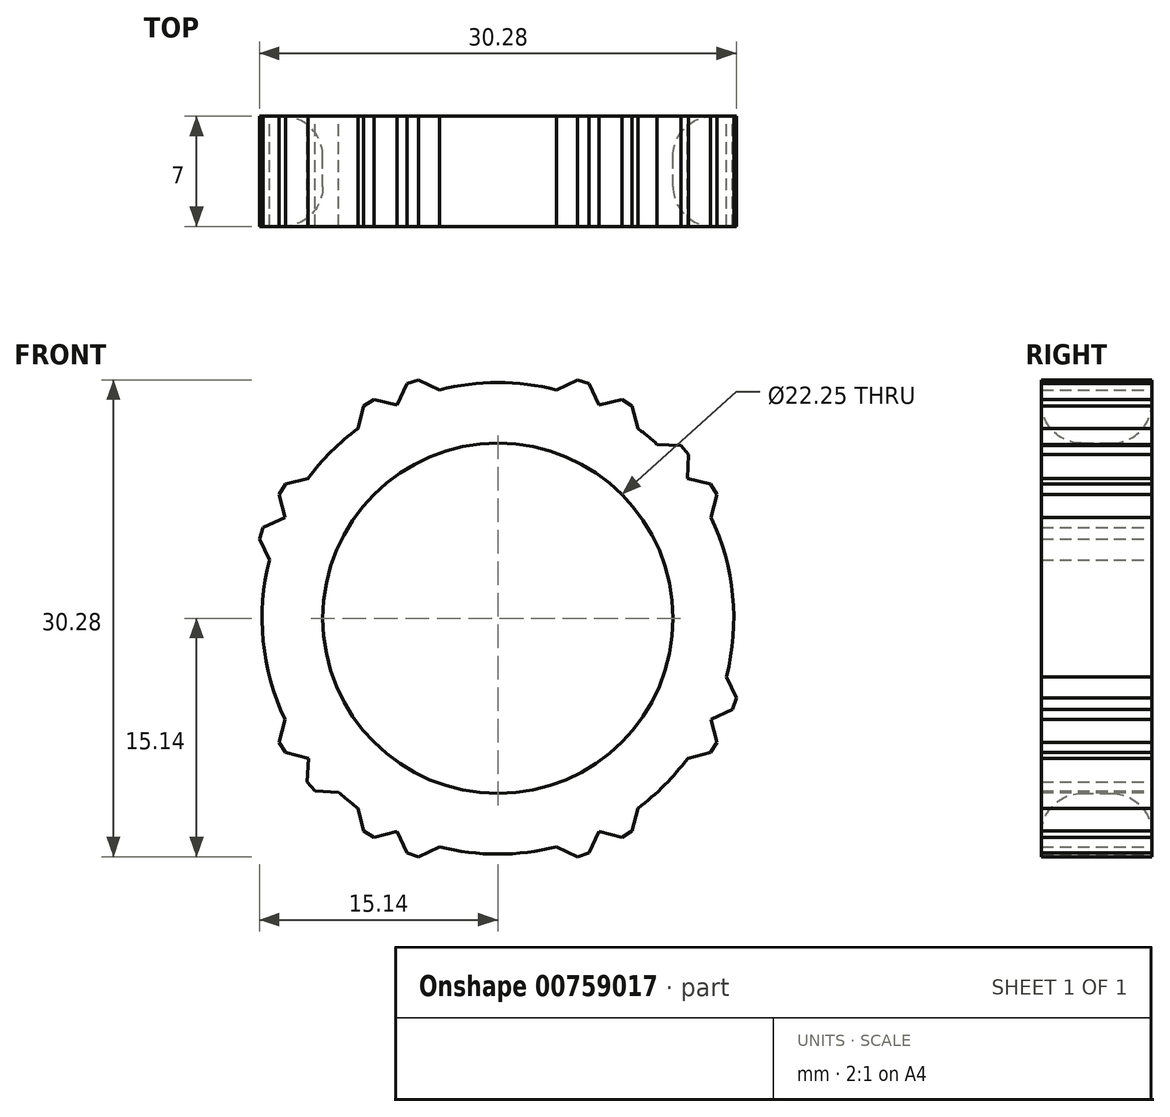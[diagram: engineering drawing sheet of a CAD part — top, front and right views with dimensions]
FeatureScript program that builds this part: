
annotation { "Feature Type Name" : "Feature", "Feature Type Description" : "" }
export const myFeature = defineFeature(function(context is Context, id is Id, definition is map)
    precondition{}
    {
        {
            var Q0;
            Q0=qCreatedBy(makeId("Front.planeOp"),FACE);
            var sketch = newSketch(context, id + "F0", { "sketchPlane" : qUnion([Q0])});
            skCircle(sketch, "E0", {"center": v(0, 0) * mm, "radius": 11.13 * mm});
            skCircle(sketch, "E1", {"center": v(0, 0) * mm, "radius": 14.98 * mm});
            skLineSegment(sketch, "E2", {"start": v(13.53, 6.42) * mm, "end": v(13.9, 7.88) * mm});
            skLineSegment(sketch, "E3", {"start": v(13.5, 8.52) * mm, "end": v(12.03, 8.89) * mm});
            skLineSegment(sketch, "E4", {"start": v(13.5, 8.52) * mm, "end": v(13.9, 7.88) * mm});
            skLineSegment(sketch, "E5.MirrorCS", {"start": v(-13.5, 8.52) * mm, "end": v(-12.03, 8.89) * mm});
            skLineSegment(sketch, "E6.MirrorCS", {"start": v(-13.53, 6.42) * mm, "end": v(-13.9, 7.88) * mm});
            skLineSegment(sketch, "E7.MirrorCS", {"start": v(-13.5, 8.52) * mm, "end": v(-13.9, 7.88) * mm});
            skLineSegment(sketch, "E8.MirrorCS", {"start": v(13.5, -8.52) * mm, "end": v(12.03, -8.89) * mm});
            skLineSegment(sketch, "E9.MirrorCS", {"start": v(13.53, -6.42) * mm, "end": v(13.9, -7.88) * mm});
            skLineSegment(sketch, "E10.MirrorCS", {"start": v(13.5, -8.52) * mm, "end": v(13.9, -7.88) * mm});
            skLineSegment(sketch, "E11.MirrorCS", {"start": v(-13.5, -8.52) * mm, "end": v(-12.03, -8.89) * mm});
            skLineSegment(sketch, "E12.MirrorCS", {"start": v(-13.53, -6.42) * mm, "end": v(-13.9, -7.88) * mm});
            skLineSegment(sketch, "E13.MirrorCS", {"start": v(-13.5, -8.52) * mm, "end": v(-13.9, -7.88) * mm});
            skLineSegment(sketch, "E14.MirrorCS", {"start": v(8.52, 13.5) * mm, "end": v(8.89, 12.03) * mm});
            skLineSegment(sketch, "E15.MirrorCS", {"start": v(6.42, 13.53) * mm, "end": v(7.88, 13.9) * mm});
            skLineSegment(sketch, "E16.MirrorCS", {"start": v(8.52, 13.5) * mm, "end": v(7.88, 13.9) * mm});
            skLineSegment(sketch, "E17.MirrorCS", {"start": v(-6.42, 13.53) * mm, "end": v(-7.88, 13.9) * mm});
            skLineSegment(sketch, "E18.MirrorCS", {"start": v(-8.52, 13.5) * mm, "end": v(-8.89, 12.03) * mm});
            skLineSegment(sketch, "E19.MirrorCS", {"start": v(-8.52, 13.5) * mm, "end": v(-7.88, 13.9) * mm});
            skLineSegment(sketch, "E20.MirrorCS", {"start": v(-8.52, -13.5) * mm, "end": v(-8.89, -12.03) * mm});
            skLineSegment(sketch, "E21.MirrorCS", {"start": v(-8.52, -13.5) * mm, "end": v(-7.88, -13.9) * mm});
            skLineSegment(sketch, "E22.MirrorCS", {"start": v(-6.42, -13.53) * mm, "end": v(-7.88, -13.9) * mm});
            skLineSegment(sketch, "E23.MirrorCS", {"start": v(8.52, -13.5) * mm, "end": v(8.89, -12.03) * mm});
            skLineSegment(sketch, "E24.MirrorCS", {"start": v(6.42, -13.53) * mm, "end": v(7.88, -13.9) * mm});
            skLineSegment(sketch, "E25.MirrorCS", {"start": v(8.52, -13.5) * mm, "end": v(7.88, -13.9) * mm});
            skLineSegment(sketch, "E26.MirrorCS", {"start": v(5.05, 15.14) * mm, "end": v(3.69, 14.5) * mm});
            skLineSegment(sketch, "E27.MirrorCS", {"start": v(6.42, 13.53) * mm, "end": v(5.78, 14.9) * mm});
            skLineSegment(sketch, "E28.MirrorCS", {"start": v(5.05, 15.14) * mm, "end": v(5.78, 14.9) * mm});
            skLineSegment(sketch, "E29.MirrorCS", {"start": v(-5.05, -15.14) * mm, "end": v(-5.78, -14.9) * mm});
            skLineSegment(sketch, "E30.MirrorCS", {"start": v(-6.42, -13.53) * mm, "end": v(-5.78, -14.9) * mm});
            skLineSegment(sketch, "E31.MirrorCS", {"start": v(-5.05, -15.14) * mm, "end": v(-3.69, -14.5) * mm});
            skLineSegment(sketch, "E32.MirrorCS", {"start": v(-5.05, 15.14) * mm, "end": v(-3.69, 14.5) * mm});
            skLineSegment(sketch, "E33.MirrorCS", {"start": v(-6.42, 13.53) * mm, "end": v(-5.78, 14.9) * mm});
            skLineSegment(sketch, "E34.MirrorCS", {"start": v(-5.05, 15.14) * mm, "end": v(-5.78, 14.9) * mm});
            skLineSegment(sketch, "E35.MirrorCS", {"start": v(5.05, -15.14) * mm, "end": v(3.69, -14.5) * mm});
            skLineSegment(sketch, "E36.MirrorCS", {"start": v(6.42, -13.53) * mm, "end": v(5.78, -14.9) * mm});
            skLineSegment(sketch, "E37.MirrorCS", {"start": v(5.05, -15.14) * mm, "end": v(5.78, -14.9) * mm});
            skLineSegment(sketch, "E38.MirrorCS", {"start": v(-13.53, 6.42) * mm, "end": v(-14.9, 5.78) * mm});
            skLineSegment(sketch, "E39.MirrorCS", {"start": v(-15.14, 5.05) * mm, "end": v(-14.9, 5.78) * mm});
            skLineSegment(sketch, "E40.MirrorCS", {"start": v(-15.14, 5.05) * mm, "end": v(-14.5, 3.69) * mm});
            skLineSegment(sketch, "E41.MirrorCS", {"start": v(15.14, -5.05) * mm, "end": v(14.5, -3.69) * mm});
            skLineSegment(sketch, "E42.MirrorCS", {"start": v(15.14, -5.05) * mm, "end": v(14.9, -5.78) * mm});
            skLineSegment(sketch, "E43.MirrorCS", {"start": v(13.53, -6.42) * mm, "end": v(14.9, -5.78) * mm});
            skLineSegment(sketch, "E44.MirrorCS", {"start": v(10.11, 11.05) * mm, "end": v(11.62, 10.98) * mm});
            skLineSegment(sketch, "E45.MirrorCS", {"start": v(12.11, 10.4) * mm, "end": v(12.03, 8.89) * mm});
            skLineSegment(sketch, "E46.MirrorCS", {"start": v(12.11, 10.4) * mm, "end": v(11.62, 10.98) * mm});
            skLineSegment(sketch, "E47.MirrorCS", {"start": v(-12.11, -10.4) * mm, "end": v(-12.03, -8.89) * mm});
            skLineSegment(sketch, "E48.MirrorCS", {"start": v(-12.11, -10.4) * mm, "end": v(-11.62, -10.98) * mm});
            skLineSegment(sketch, "E49.MirrorCS", {"start": v(-10.11, -11.05) * mm, "end": v(-11.62, -10.98) * mm});
            skSolve(sketch);
        }
        {
            var Q0;
            Q0=makeQuery(id+"F0.imprint","IMPRINT",FACE,{"disambiguationData":[TD([[makeQuery(id+"F0.imprint","IMPRINT",EDGE,{"derivedFrom":sQuery(id+"F0.wireOp",EDGE,"E0")}),-1.0]])]});
            var Q1;
            {var subQ4=sQuery(id+"F0.wireOp",EDGE,"E48.MirrorCS");Q1=makeQuery(id+"F0.imprint","IMPRINT",FACE,{"disambiguationData":[TD([[makeQuery(id+"F0.imprint","IMPRINT",EDGE,{"derivedFrom":subQ4}),1.0]])]});}
            var Q2;
            {var subQ0=sQuery(id+"F0.wireOp",EDGE,"E12.MirrorCS");Q2=makeQuery(id+"F0.imprint","IMPRINT",FACE,{"disambiguationData":[TD([[makeQuery(id+"F0.imprint","IMPRINT",EDGE,{"derivedFrom":subQ0}),1.0]])]});}
            var Q3;
            {var subQ4=sQuery(id+"F0.wireOp",EDGE,"E21.MirrorCS");Q3=makeQuery(id+"F0.imprint","IMPRINT",FACE,{"disambiguationData":[TD([[makeQuery(id+"F0.imprint","IMPRINT",EDGE,{"derivedFrom":subQ4}),1.0]])]});}
            var Q4;
            {var subQ4=sQuery(id+"F0.wireOp",EDGE,"E29.MirrorCS");Q4=makeQuery(id+"F0.imprint","IMPRINT",FACE,{"disambiguationData":[TD([[makeQuery(id+"F0.imprint","IMPRINT",EDGE,{"derivedFrom":subQ4}),-1.0]])]});}
            var Q5;
            {var subQ0=sQuery(id+"F0.wireOp",EDGE,"E36.MirrorCS");Q5=makeQuery(id+"F0.imprint","IMPRINT",FACE,{"disambiguationData":[TD([[makeQuery(id+"F0.imprint","IMPRINT",EDGE,{"derivedFrom":subQ0}),-1.0]])]});}
            var Q6;
            {var subQ0=sQuery(id+"F0.wireOp",EDGE,"E24.MirrorCS");Q6=makeQuery(id+"F0.imprint","IMPRINT",FACE,{"disambiguationData":[TD([[makeQuery(id+"F0.imprint","IMPRINT",EDGE,{"derivedFrom":subQ0}),1.0]])]});}
            var Q7;
            {var subQ0=sQuery(id+"F0.wireOp",EDGE,"E9.MirrorCS");Q7=makeQuery(id+"F0.imprint","IMPRINT",FACE,{"disambiguationData":[TD([[makeQuery(id+"F0.imprint","IMPRINT",EDGE,{"derivedFrom":subQ0}),-1.0]])]});}
            var Q8;
            {var subQ4=sQuery(id+"F0.wireOp",EDGE,"E42.MirrorCS");Q8=makeQuery(id+"F0.imprint","IMPRINT",FACE,{"disambiguationData":[TD([[makeQuery(id+"F0.imprint","IMPRINT",EDGE,{"derivedFrom":subQ4}),-1.0]])]});}
            var Q9;
            {var subQ0=sQuery(id+"F0.wireOp",EDGE,"E38.MirrorCS");Q9=makeQuery(id+"F0.imprint","IMPRINT",FACE,{"disambiguationData":[TD([[makeQuery(id+"F0.imprint","IMPRINT",EDGE,{"derivedFrom":subQ0}),1.0]])]});}
            var Q10;
            {var subQ0=sQuery(id+"F0.wireOp",EDGE,"E6.MirrorCS");Q10=makeQuery(id+"F0.imprint","IMPRINT",FACE,{"disambiguationData":[TD([[makeQuery(id+"F0.imprint","IMPRINT",EDGE,{"derivedFrom":subQ0}),-1.0]])]});}
            var Q11;
            {var subQ0=sQuery(id+"F0.wireOp",EDGE,"E2");Q11=makeQuery(id+"F0.imprint","IMPRINT",FACE,{"disambiguationData":[TD([[makeQuery(id+"F0.imprint","IMPRINT",EDGE,{"derivedFrom":subQ0}),1.0]])]});}
            var Q12;
            {var subQ0=sQuery(id+"F0.wireOp",EDGE,"E44.MirrorCS");Q12=makeQuery(id+"F0.imprint","IMPRINT",FACE,{"disambiguationData":[TD([[makeQuery(id+"F0.imprint","IMPRINT",EDGE,{"derivedFrom":subQ0}),-1.0]])]});}
            var Q13;
            {var subQ0=sQuery(id+"F0.wireOp",EDGE,"E15.MirrorCS");Q13=makeQuery(id+"F0.imprint","IMPRINT",FACE,{"disambiguationData":[TD([[makeQuery(id+"F0.imprint","IMPRINT",EDGE,{"derivedFrom":subQ0}),-1.0]])]});}
            var Q14;
            {var subQ0=sQuery(id+"F0.wireOp",EDGE,"E27.MirrorCS");Q14=makeQuery(id+"F0.imprint","IMPRINT",FACE,{"disambiguationData":[TD([[makeQuery(id+"F0.imprint","IMPRINT",EDGE,{"derivedFrom":subQ0}),1.0]])]});}
            var Q15;
            {var subQ4=sQuery(id+"F0.wireOp",EDGE,"E34.MirrorCS");Q15=makeQuery(id+"F0.imprint","IMPRINT",FACE,{"disambiguationData":[TD([[makeQuery(id+"F0.imprint","IMPRINT",EDGE,{"derivedFrom":subQ4}),1.0]])]});}
            var Q16;
            {var subQ0=sQuery(id+"F0.wireOp",EDGE,"E17.MirrorCS");Q16=makeQuery(id+"F0.imprint","IMPRINT",FACE,{"disambiguationData":[TD([[makeQuery(id+"F0.imprint","IMPRINT",EDGE,{"derivedFrom":subQ0}),1.0]])]});}
            extrude(context, id + "F1", {"entities" : qUnion([Q0, Q1, Q2, Q3, Q4, Q5, Q6, Q7, Q8, Q9, Q10, Q11, Q12, Q13, Q14, Q15, Q16]), "depth" : 7 * mm, "offsetDistance" : 25.4 * mm});
        }
        {
            var Q0;
            Q0=makeQuery(id+"F1.opExtrude","CAP_EDGE",EDGE,{"disambiguationData":[OSD([sQuery(id+"F0.wireOp",EDGE,"E0")])],"isStart":false});
            var Q1;
            Q1=makeQuery(id+"F1.opExtrude","CAP_EDGE",EDGE,{"disambiguationData":[OSD([sQuery(id+"F0.wireOp",EDGE,"E0")])],"isStart":true});
            fillet(context, id + "F2", {"entities" : qUnion([Q0, Q1]), "radius" : 2.54 * mm, "tangentPropagation" : true, "allowEdgeOverflow" : false});
        }
    });
